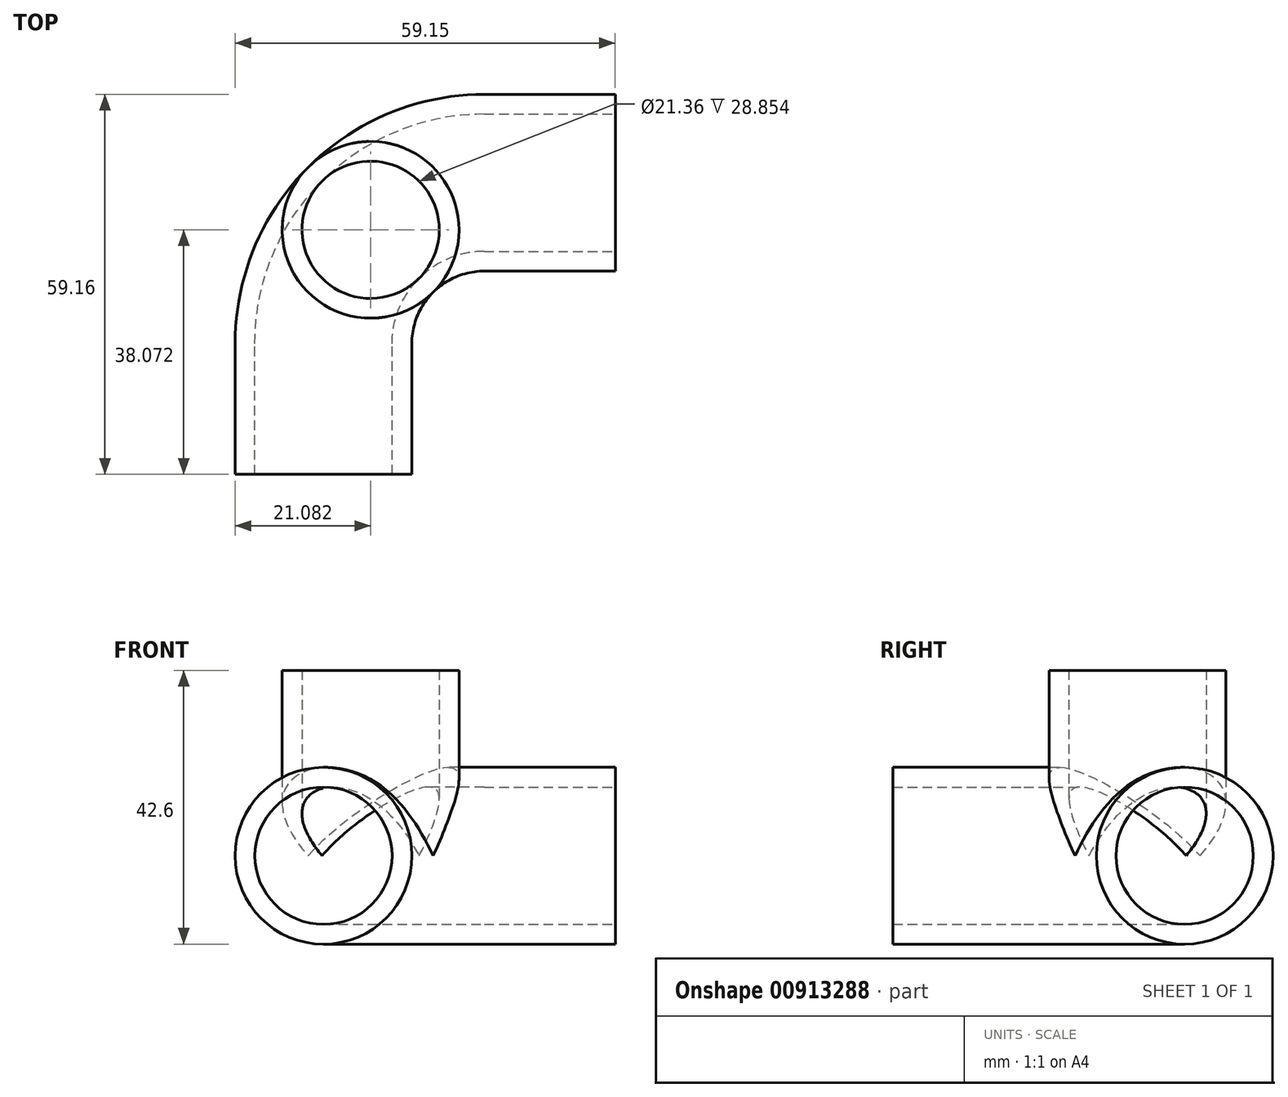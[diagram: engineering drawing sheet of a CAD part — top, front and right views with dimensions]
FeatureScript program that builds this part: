
annotation { "Feature Type Name" : "Feature", "Feature Type Description" : "" }
export const myFeature = defineFeature(function(context is Context, id is Id, definition is map)
    precondition{}
    {
        {
            var Q0;
            Q0=qCreatedBy(makeId("Front.planeOp"),FACE);
            cPlane(context, id + "F0", {"entities" : qUnion([Q0]), "cplaneType" : CPlaneType.OFFSET, "offset" : 31.65 * mm, "width" : 152.4 * mm, "height" : 152.4 * mm});
        }
        {
            var Q0;
            Q0=qCreatedBy(id+"F0.planeOp",FACE);
            var sketch = newSketch(context, id + "F1", { "sketchPlane" : qUnion([Q0])});
            skCircle(sketch, "E0", {"center": v(0, 0) * mm, "radius": 13.75 * mm});
            skCircle(sketch, "E1", {"center": v(0, 0) * mm, "radius": 10.68 * mm});
            skSolve(sketch);
        }
        {
            var Q0;
            Q0=qCreatedBy(makeId("Top.planeOp"),FACE);
            var sketch = newSketch(context, id + "F2", { "sketchPlane" : qUnion([Q0])});
            skPoint(sketch, "E2.0", {"position": v(0, -31.65) * mm});
            skLineSegment(sketch, "E3", {"start": v(0, -31.65) * mm, "end": v(0, -11.28) * mm});
            skLineSegment(sketch, "E4", {"start": v(25.03, 13.75) * mm, "end": v(45.4, 13.75) * mm});
            skPoint(sketch, "E5.visualSharp", {"position": v(0, 13.75) * mm});
            skArc(sketch, "E5.filletArc", {"start": v(25.03, 13.75) * mm, "mid": v(7.33, 6.42) * mm, "end": v(0, -11.28) * mm});
            skSolve(sketch);
        }
        {
            var Q0;
            Q0=makeQuery(id+"F1.imprint","IMPRINT",FACE,{"disambiguationData":[TD([[makeQuery(id+"F1.imprint","IMPRINT",EDGE,{"derivedFrom":sQuery(id+"F1.wireOp",EDGE,"E0")}),1.0]])]});
            var Q1;
            Q1=sQuery(id+"F2.wireOp",EDGE,"E5.filletArc");
            var Q2;
            Q2=sQuery(id+"F2.wireOp",EDGE,"E3");
            var Q3;
            Q3=sQuery(id+"F2.wireOp",EDGE,"E4");
            sweep(context, id + "F3", {"profiles" : qUnion([Q0]), "path" : qUnion([Q1, Q2, Q3])});
        }
        {
            var Q0;
            Q0=qCreatedBy(makeId("Top.planeOp"),FACE);
            var sketch = newSketch(context, id + "F4", { "sketchPlane" : qUnion([Q0])});
            skArc(sketch, "E6.0", {"start": v(25.03, 13.75) * mm, "mid": v(7.33, 6.42) * mm, "end": v(0, -11.28) * mm, "construction": true});
            skCircle(sketch, "E7", {"center": v(7.33, 6.42) * mm, "radius": 13.75 * mm});
            skCircle(sketch, "E8", {"center": v(7.33, 6.42) * mm, "radius": 10.68 * mm});
            skSolve(sketch);
        }
        {
            var Q0;
            Q0=makeQuery(id+"F4.imprint","IMPRINT",FACE,{"disambiguationData":[TD([[makeQuery(id+"F4.imprint","IMPRINT",EDGE,{"derivedFrom":sQuery(id+"F4.wireOp",EDGE,"E7")}),1.0]])]});
            extrude(context, id + "F5", {"entities" : qUnion([Q0]), "operationType" : NewBodyOperationType.ADD, "depth" : 28.85 * mm, "offsetDistance" : 25.4 * mm});
        }
        {
            var Q0;
            Q0=makeQuery(id+"F1.imprint","IMPRINT",FACE,{"disambiguationData":[TD([[makeQuery(id+"F1.imprint","IMPRINT",EDGE,{"derivedFrom":sQuery(id+"F1.wireOp",EDGE,"E1")}),1.0]])]});
            var Q1;
            Q1=sQuery(id+"F2.wireOp",EDGE,"E4");
            var Q2;
            Q2=sQuery(id+"F2.wireOp",EDGE,"E5.filletArc");
            var Q3;
            Q3=sQuery(id+"F2.wireOp",EDGE,"E3");
            sweep(context, id + "F6", {"operationType" : NewBodyOperationType.REMOVE, "profiles" : qUnion([Q0]), "path" : qUnion([Q1, Q2, Q3])});
        }
        {
            var Q0;
            Q0=makeQuery(id+"F4.imprint","IMPRINT",FACE,{"disambiguationData":[TD([[makeQuery(id+"F4.imprint","IMPRINT",EDGE,{"derivedFrom":sQuery(id+"F4.wireOp",EDGE,"E8")}),1.0]])]});
            extrude(context, id + "F7", {"entities" : qUnion([Q0]), "operationType" : NewBodyOperationType.REMOVE, "depth" : 25.4 * mm, "offsetDistance" : 25.4 * mm});
        }
    });
